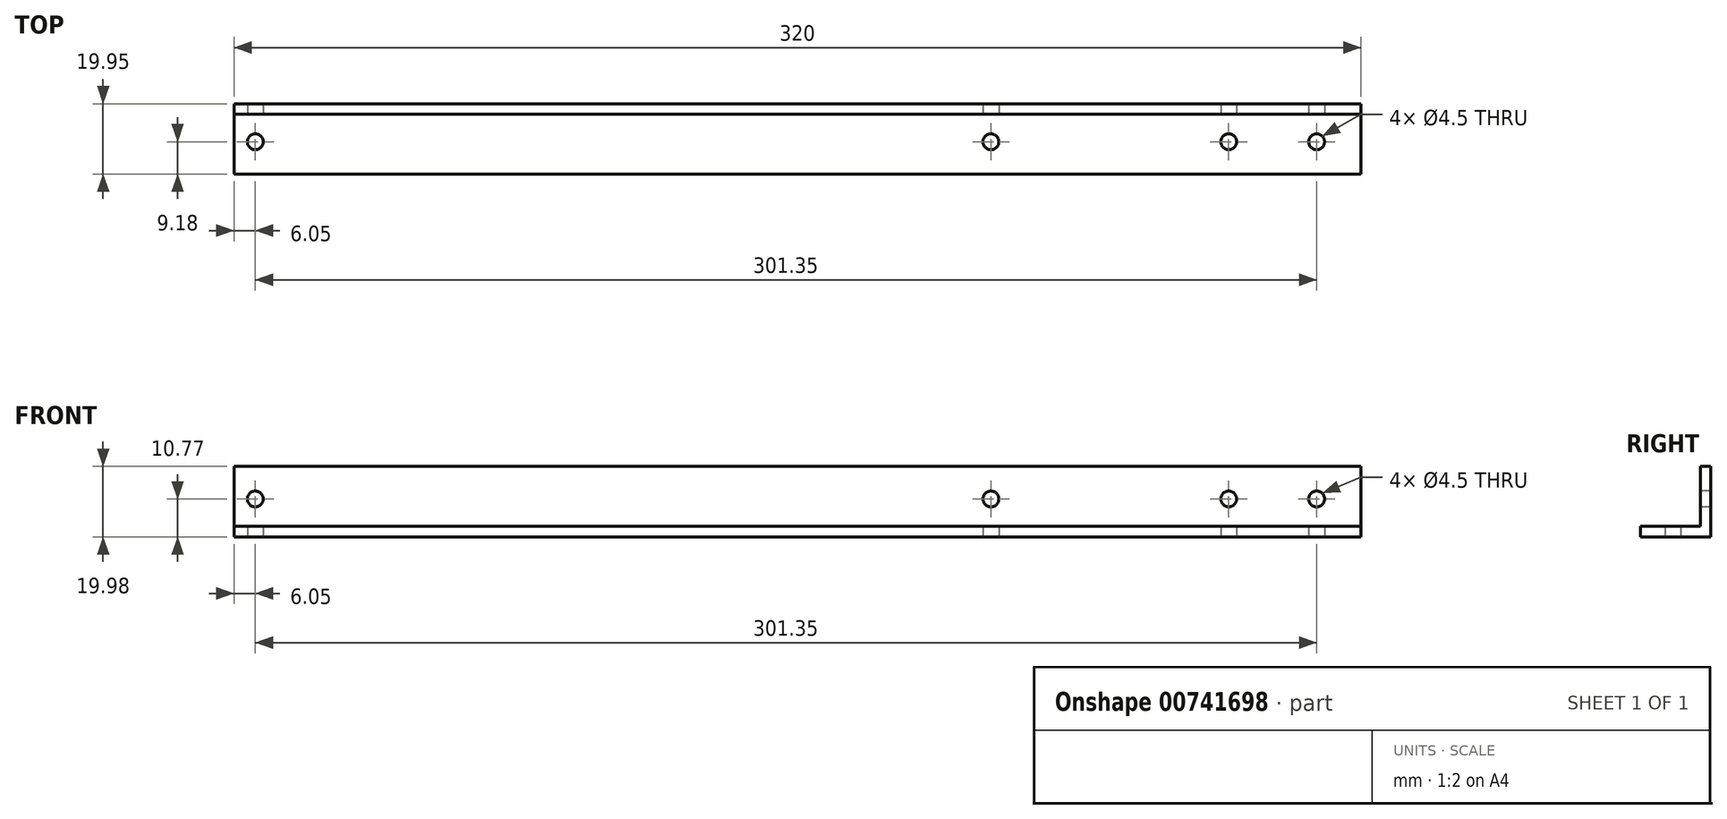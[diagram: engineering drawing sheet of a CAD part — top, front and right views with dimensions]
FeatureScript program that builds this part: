
annotation { "Feature Type Name" : "Feature", "Feature Type Description" : "" }
export const myFeature = defineFeature(function(context is Context, id is Id, definition is map)
    precondition{}
    {
        {
            var Q0;
            Q0=qCreatedBy(makeId("Top.planeOp"),FACE);
            var sketch = newSketch(context, id + "F0", { "sketchPlane" : qUnion([Q0])});
            skLineSegment(sketch, "E0.bottom", {"start": v(0, 0) * mm, "end": v(320, 0) * mm});
            skLineSegment(sketch, "E0.top", {"start": v(0, 19.95) * mm, "end": v(320, 19.95) * mm});
            skLineSegment(sketch, "E0.left", {"start": v(0, 0) * mm, "end": v(0, 19.95) * mm});
            skLineSegment(sketch, "E0.right", {"start": v(320, 0) * mm, "end": v(320, 19.95) * mm});
            skLineSegment(sketch, "E1", {"start": v(0, 9.18) * mm, "end": v(320, 9.18) * mm, "construction": true});
            skCircle(sketch, "E2", {"center": v(307.4, 9.18) * mm, "radius": 2.25 * mm});
            skCircle(sketch, "E3", {"center": v(282.43, 9.18) * mm, "radius": 2.25 * mm});
            skCircle(sketch, "E4", {"center": v(214.92, 9.18) * mm, "radius": 2.25 * mm});
            skCircle(sketch, "E5", {"center": v(6.05, 9.18) * mm, "radius": 2.25 * mm});
            skSolve(sketch);
        }
        {
            var Q0;
            Q0=makeQuery(id+"F0.imprint","IMPRINT",FACE,{"disambiguationData":[TD([[makeQuery(id+"F0.imprint","IMPRINT",EDGE,{"derivedFrom":sQuery(id+"F0.wireOp",EDGE,"E0.bottom")}),1.0]])]});
            extrude(context, id + "F1", {"entities" : qUnion([Q0]), "depth" : 3 * mm, "offsetDistance" : 25 * mm});
        }
        {
            var Q0;
            Q0=makeQuery(id+"F1.opExtrude","CAP_FACE",FACE,{"disambiguationData":[OSD([sQuery(id+"F0.wireOp",EDGE,"E0.bottom"),sQuery(id+"F0.wireOp",EDGE,"E0.top"),sQuery(id+"F0.wireOp",EDGE,"E0.left"),sQuery(id+"F0.wireOp",EDGE,"E0.right"),sQuery(id+"F0.wireOp",EDGE,"E2"),sQuery(id+"F0.wireOp",EDGE,"E3"),sQuery(id+"F0.wireOp",EDGE,"E4"),sQuery(id+"F0.wireOp",EDGE,"E5")])],"isStart":false});
            var sketch = newSketch(context, id + "F2", { "sketchPlane" : qUnion([Q0])});
            skLineSegment(sketch, "E6", {"start": v(0, 16.95) * mm, "end": v(320, 16.95) * mm});
            skLineSegment(sketch, "E7", {"start": v(6.05, 9.18) * mm, "end": v(0, 9.18) * mm, "construction": true});
            skSolve(sketch);
        }
        {
            var Q0;
            {var subQ0=sQuery(id+"F2.wireOp",EDGE,"E6");Q0=makeQuery(id+"F2.imprint","IMPRINT",FACE,{"disambiguationData":[TD([[makeQuery(id+"F2.imprint","IMPRINT",EDGE,{"derivedFrom":subQ0}),1.0]])]});}
            extrude(context, id + "F3", {"entities" : qUnion([Q0]), "operationType" : NewBodyOperationType.ADD, "depth" : 16.98 * mm, "offsetDistance" : 25 * mm});
        }
        {
            var Q0;
            Q0=makeQuery(id+"F3.opExtrude","SWEPT_FACE",FACE,{"disambiguationData":[OSD([sQuery(id+"F2.wireOp",EDGE,"E6")])]});
            var sketch = newSketch(context, id + "F4", { "sketchPlane" : qUnion([Q0])});
            skSolve(sketch);
        }
        {
            var Q0;
            Q0=makeQuery(id+"F1.opExtrude","CAP_FACE",FACE,{"disambiguationData":[OSD([sQuery(id+"F0.wireOp",EDGE,"E0.bottom"),sQuery(id+"F0.wireOp",EDGE,"E0.top"),sQuery(id+"F0.wireOp",EDGE,"E0.left"),sQuery(id+"F0.wireOp",EDGE,"E0.right"),sQuery(id+"F0.wireOp",EDGE,"E2"),sQuery(id+"F0.wireOp",EDGE,"E3"),sQuery(id+"F0.wireOp",EDGE,"E4"),sQuery(id+"F0.wireOp",EDGE,"E5")])],"isStart":false});
            var sketch = newSketch(context, id + "F5", { "sketchPlane" : qUnion([Q0])});
            skLineSegment(sketch, "E8", {"start": v(307.4, 9.18) * mm, "end": v(307.4, 16.95) * mm, "construction": true});
            skLineSegment(sketch, "E9", {"start": v(282.43, 9.18) * mm, "end": v(282.43, 16.95) * mm, "construction": true});
            skLineSegment(sketch, "E10", {"start": v(214.92, 9.18) * mm, "end": v(214.92, 16.95) * mm, "construction": true});
            skLineSegment(sketch, "E11", {"start": v(6.05, 9.18) * mm, "end": v(6.05, 16.95) * mm, "construction": true});
            skSolve(sketch);
        }
        {
            var Q0;
            {var subQ0=sQuery(id+"F2.wireOp",EDGE,"E6");Q0=makeQuery(id+"F4.imprint","IMPRINT",FACE,{"disambiguationData":[TD([[makeQuery(id+"F4.imprint","IMPRINT",EDGE,{"derivedFrom":makeQuery(id+"F3.opExtrude","CAP_EDGE",EDGE,{"disambiguationData":[OSD([subQ0])],"isStart":false})}),-1.0]])]});}
            var sketch = newSketch(context, id + "F6", { "sketchPlane" : qUnion([Q0])});
            skPoint(sketch, "E12.0", {"position": v(6.05, 3) * mm});
            skLineSegment(sketch, "E13", {"start": v(6.05, 3) * mm, "end": v(6.05, 20) * mm, "construction": true});
            skLineSegment(sketch, "E14", {"start": v(0, 10.77) * mm, "end": v(320, 10.77) * mm, "construction": true});
            skCircle(sketch, "E15", {"center": v(6.05, 10.77) * mm, "radius": 2.25 * mm});
            skPoint(sketch, "E16.0", {"position": v(214.92, 3) * mm});
            skLineSegment(sketch, "E17", {"start": v(214.92, 3) * mm, "end": v(214.92, 19.87) * mm, "construction": true});
            skCircle(sketch, "E18", {"center": v(214.92, 10.77) * mm, "radius": 2.25 * mm});
            skPoint(sketch, "E19.0", {"position": v(282.43, 3) * mm});
            skLineSegment(sketch, "E20", {"start": v(282.43, 3) * mm, "end": v(282.43, 20.04) * mm, "construction": true});
            skPoint(sketch, "E21.0", {"position": v(307.4, 3) * mm});
            skLineSegment(sketch, "E22", {"start": v(307.4, 3.17) * mm, "end": v(307.4, 19.9) * mm, "construction": true});
            skCircle(sketch, "E23", {"center": v(307.4, 10.77) * mm, "radius": 2.25 * mm});
            skCircle(sketch, "E24", {"center": v(282.43, 10.77) * mm, "radius": 2.25 * mm});
            skSolve(sketch);
        }
        {
            var Q0;
            Q0=makeQuery(id+"F6.imprint","IMPRINT",FACE,{"disambiguationData":[TD([[makeQuery(id+"F6.imprint","IMPRINT",EDGE,{"derivedFrom":sQuery(id+"F6.wireOp",EDGE,"E23")}),1.0]])]});
            var Q1;
            Q1=makeQuery(id+"F6.imprint","IMPRINT",FACE,{"disambiguationData":[TD([[makeQuery(id+"F6.imprint","IMPRINT",EDGE,{"derivedFrom":sQuery(id+"F6.wireOp",EDGE,"E24")}),1.0]])]});
            var Q2;
            Q2=makeQuery(id+"F6.imprint","IMPRINT",FACE,{"disambiguationData":[TD([[makeQuery(id+"F6.imprint","IMPRINT",EDGE,{"derivedFrom":sQuery(id+"F6.wireOp",EDGE,"E18")}),1.0]])]});
            var Q3;
            Q3=makeQuery(id+"F6.imprint","IMPRINT",FACE,{"disambiguationData":[TD([[makeQuery(id+"F6.imprint","IMPRINT",EDGE,{"derivedFrom":sQuery(id+"F6.wireOp",EDGE,"E15")}),1.0]])]});
            extrude(context, id + "F7", {"entities" : qUnion([Q0, Q1, Q2, Q3]), "operationType" : NewBodyOperationType.REMOVE, "endBound" : BoundingType.THROUGH_ALL, "oppositeDirection" : true, "depth" : 25 * mm, "offsetDistance" : 25 * mm});
        }
    });
